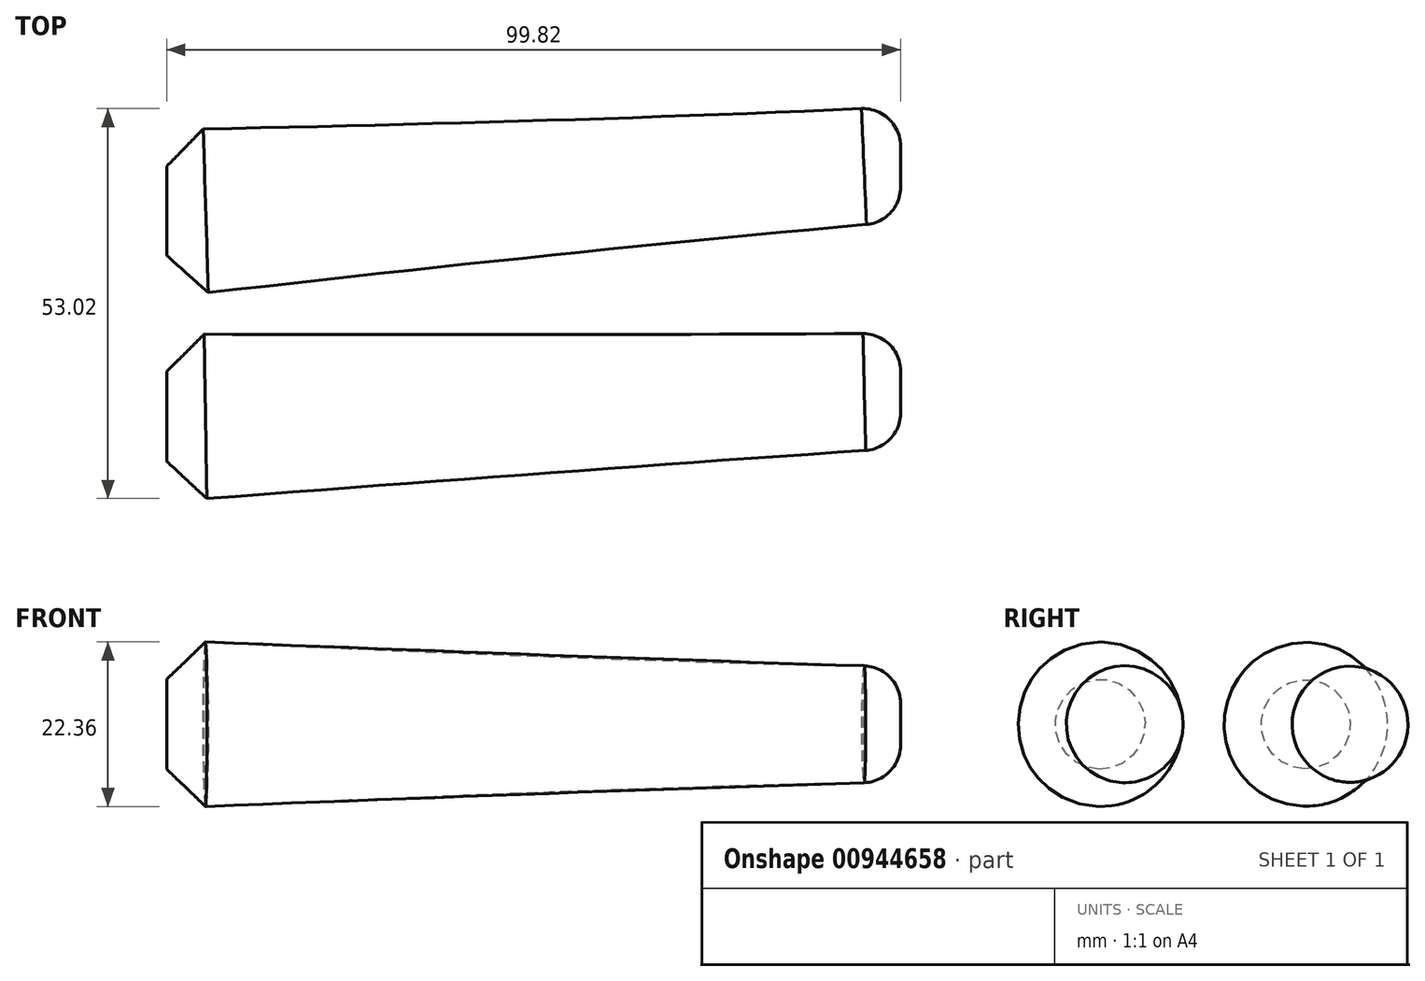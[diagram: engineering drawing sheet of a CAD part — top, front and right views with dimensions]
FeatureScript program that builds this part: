
annotation { "Feature Type Name" : "Feature", "Feature Type Description" : "" }
export const myFeature = defineFeature(function(context is Context, id is Id, definition is map)
    precondition{}
    {
        {
            var Q0;
            Q0=qCreatedBy(makeId("Right.planeOp"),FACE);
            cPlane(context, id + "F0", {"entities" : qUnion([Q0]), "cplaneType" : CPlaneType.OFFSET, "offset" : 99.82 * mm, "width" : 152.4 * mm, "height" : 152.4 * mm});
        }
        {
            var Q0;
            Q0=qCreatedBy(makeId("Right.planeOp"),FACE);
            var sketch = newSketch(context, id + "F1", { "sketchPlane" : qUnion([Q0])});
            skCircle(sketch, "E0", {"center": v(0, 0) * mm, "radius": 11.4 * mm});
            skSolve(sketch);
        }
        {
            var Q0;
            Q0=qCreatedBy(id+"F0.planeOp",FACE);
            var sketch = newSketch(context, id + "F2", { "sketchPlane" : qUnion([Q0])});
            skCircle(sketch, "E1", {"center": v(6.71, 0) * mm, "radius": 7.8 * mm});
            skSolve(sketch);
        }
        {
            var Q0;
            Q0=makeQuery(id+"F1.imprint","IMPRINT",FACE,{"disambiguationData":[TD([[makeQuery(id+"F1.imprint","IMPRINT",EDGE,{"derivedFrom":sQuery(id+"F1.wireOp",EDGE,"E0")}),1.0]])]});
            var Q1;
            Q1=makeQuery(id+"F2.imprint","IMPRINT",FACE,{"disambiguationData":[TD([[makeQuery(id+"F2.imprint","IMPRINT",EDGE,{"derivedFrom":sQuery(id+"F2.wireOp",EDGE,"E1")}),1.0]])]});
            loft(context, id + "F3", {"sheetProfilesArray" : [{ "sheetProfileEntities" : qUnion([Q0]) }, { "sheetProfileEntities" : qUnion([Q1]) }]});
        }
        {
            var Q0;
            Q0=qCreatedBy(makeId("Top.planeOp"),FACE);
            cPlane(context, id + "F4", {"entities" : qUnion([Q0]), "cplaneType" : CPlaneType.OFFSET, "offset" : 22.86 * mm, "width" : 152.4 * mm, "height" : 152.4 * mm});
        }
        {
            var Q0;
            Q0=makeQuery(id+"F3.opLoft","CAP_FACE",FACE,{"disambiguationData":[OSD([makeQuery(id+"F2.imprint","IMPRINT",FACE,{"disambiguationData":[TD([[makeQuery(id+"F2.imprint","IMPRINT",EDGE,{"derivedFrom":sQuery(id+"F2.wireOp",EDGE,"E1")}),1.0]])]})])],"isStart":true});
            fillet(context, id + "F5", {"entities" : qUnion([Q0]), "radius" : 5.08 * mm, "tangentPropagation" : true, "allowEdgeOverflow" : false});
        }
        {
            var Q0;
            Q0=makeQuery(id+"F3.opLoft","MID_CAP_EDGE",EDGE,{"disambiguationData":[OSD([sQuery(id+"F1.wireOp",EDGE,"E0")])],"capPos":0.0});
            chamfer(context, id + "F6", {"entities" : qUnion([Q0]), "width" : 5.08 * mm, "tangentPropagation" : true});
        }
        {
            var Q0;
            Q0=qCreatedBy(makeId("Right.planeOp"),FACE);
            var sketch = newSketch(context, id + "F7", { "sketchPlane" : qUnion([Q0])});
            skCircle(sketch, "E2", {"center": v(-27.78, 0) * mm, "radius": 11.4 * mm});
            skSolve(sketch);
        }
        {
            var Q0;
            Q0=qCreatedBy(id+"F0.planeOp",FACE);
            var sketch = newSketch(context, id + "F8", { "sketchPlane" : qUnion([Q0])});
            skCircle(sketch, "E3", {"center": v(-24.09, 0) * mm, "radius": 7.8 * mm});
            skSolve(sketch);
        }
        {
            var Q0;
            Q0=makeQuery(id+"F7.imprint","IMPRINT",FACE,{"disambiguationData":[TD([[makeQuery(id+"F7.imprint","IMPRINT",EDGE,{"derivedFrom":sQuery(id+"F7.wireOp",EDGE,"E2")}),1.0]])]});
            var Q1;
            Q1=makeQuery(id+"F8.imprint","IMPRINT",FACE,{"disambiguationData":[TD([[makeQuery(id+"F8.imprint","IMPRINT",EDGE,{"derivedFrom":sQuery(id+"F8.wireOp",EDGE,"E3")}),1.0]])]});
            loft(context, id + "F9", {"sheetProfilesArray" : [{ "sheetProfileEntities" : qUnion([Q0]) }, { "sheetProfileEntities" : qUnion([Q1]) }]});
        }
        {
            var Q0;
            Q0=makeQuery(id+"F9.opLoft","CAP_FACE",FACE,{"disambiguationData":[OSD([makeQuery(id+"F7.imprint","IMPRINT",FACE,{"disambiguationData":[TD([[makeQuery(id+"F7.imprint","IMPRINT",EDGE,{"derivedFrom":sQuery(id+"F7.wireOp",EDGE,"E2")}),1.0]])]})])],"isStart":true});
            chamfer(context, id + "F10", {"entities" : qUnion([Q0]), "width" : 5.08 * mm, "tangentPropagation" : true});
        }
        {
            var Q0;
            Q0=makeQuery(id+"F9.opLoft","CAP_FACE",FACE,{"disambiguationData":[OSD([makeQuery(id+"F8.imprint","IMPRINT",FACE,{"disambiguationData":[TD([[makeQuery(id+"F8.imprint","IMPRINT",EDGE,{"derivedFrom":sQuery(id+"F8.wireOp",EDGE,"E3")}),1.0]])]})])],"isStart":true});
            fillet(context, id + "F11", {"entities" : qUnion([Q0]), "radius" : 5.08 * mm, "tangentPropagation" : true, "allowEdgeOverflow" : false});
        }
    });
